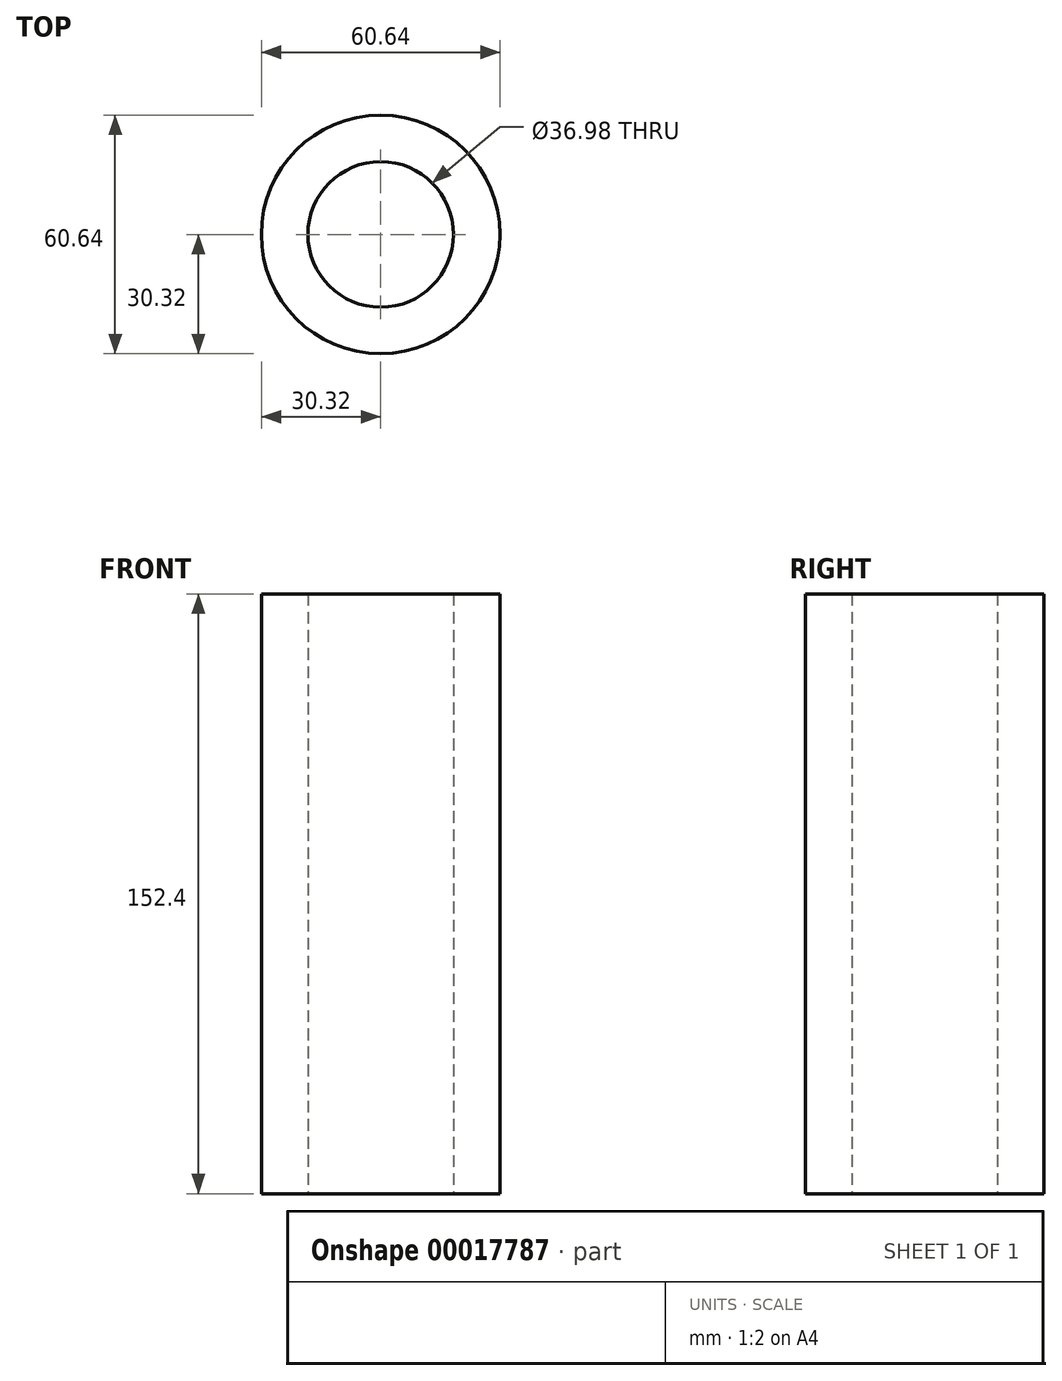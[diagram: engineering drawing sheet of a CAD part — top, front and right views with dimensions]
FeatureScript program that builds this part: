
annotation { "Feature Type Name" : "Feature", "Feature Type Description" : "" }
export const myFeature = defineFeature(function(context is Context, id is Id, definition is map)
    precondition{}
    {
        {
            var Q0;
            Q0=qCreatedBy(makeId("Top.planeOp"),FACE);
            var sketch = newSketch(context, id + "F0", { "sketchPlane" : qUnion([Q0])});
            skCircle(sketch, "E0", {"center": v(0, 0) * mm, "radius": 18.5 * mm});
            skCircle(sketch, "E1", {"center": v(0, 0) * mm, "radius": 30.32 * mm});
            skSolve(sketch);
        }
        {
            var Q0;
            Q0=makeQuery(id+"F0.imprint","IMPRINT",FACE,{"disambiguationData":[TD([[makeQuery(id+"F0.imprint","IMPRINT",EDGE,{"derivedFrom":sQuery(id+"F0.wireOp",EDGE,"E0")}),1.0]])]});
            extrude(context, id + "F1", {"entities" : qUnion([Q0]), "depth" : 152.4 * mm});
        }
        {
            var Q0;
            Q0=makeQuery(id+"F0.imprint","IMPRINT",FACE,{"disambiguationData":[TD([[makeQuery(id+"F0.imprint","IMPRINT",EDGE,{"derivedFrom":sQuery(id+"F0.wireOp",EDGE,"E0")}),-1.0]])]});
            extrude(context, id + "F2", {"entities" : qUnion([Q0]), "depth" : 152.4 * mm});
        }
    });
